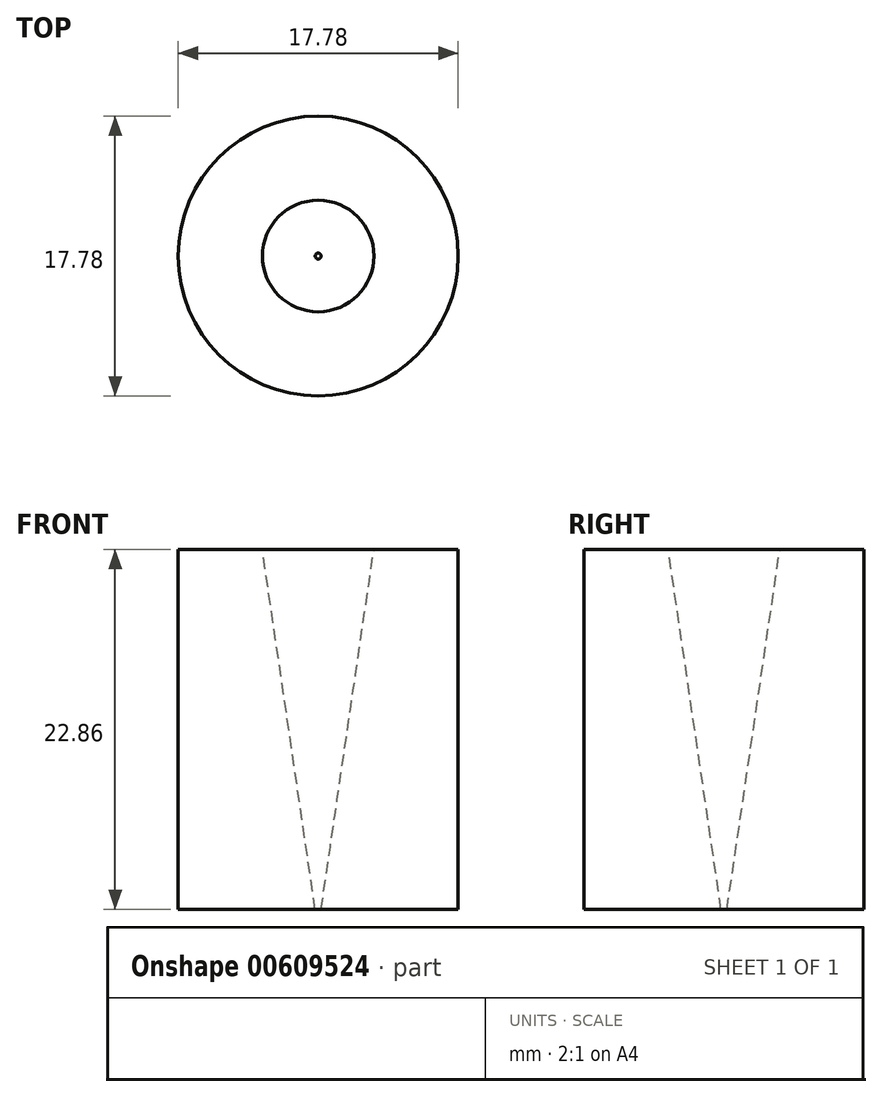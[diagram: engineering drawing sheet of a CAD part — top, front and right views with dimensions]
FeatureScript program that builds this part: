
annotation { "Feature Type Name" : "Feature", "Feature Type Description" : "" }
export const myFeature = defineFeature(function(context is Context, id is Id, definition is map)
    precondition{}
    {
        {
            var Q0;
            Q0=qCreatedBy(makeId("Front.planeOp"),FACE);
            var sketch = newSketch(context, id + "F0", { "sketchPlane" : qUnion([Q0])});
            skLineSegment(sketch, "E0", {"start": v(0.19, 0) * mm, "end": v(3.54, 22.86) * mm});
            skLineSegment(sketch, "E1", {"start": v(0.19, 0) * mm, "end": v(0, -1.27) * mm, "construction": true});
            skLineSegment(sketch, "E2", {"start": v(0.19, 0) * mm, "end": v(8.9, 0) * mm});
            skLineSegment(sketch, "E3", {"start": v(8.9, 0) * mm, "end": v(8.9, 22.86) * mm});
            skLineSegment(sketch, "E4", {"start": v(8.9, 22.86) * mm, "end": v(3.54, 22.86) * mm});
            skLineSegment(sketch, "E5", {"start": v(0, 24.52) * mm, "end": v(0, -5.3) * mm, "construction": true});
            skSolve(sketch);
        }
        {
            var Q0;
            Q0 = qSketchRegion(id + "F0", true);
            var Q1;
            Q1=sQuery(id+"F0.wireOp",EDGE,"E5");
            revolve(context, id + "F1", {"entities" : qUnion([Q0]), "axis" : qUnion([Q1]), "revolveType" : RevolveType.FULL});
        }
    });
